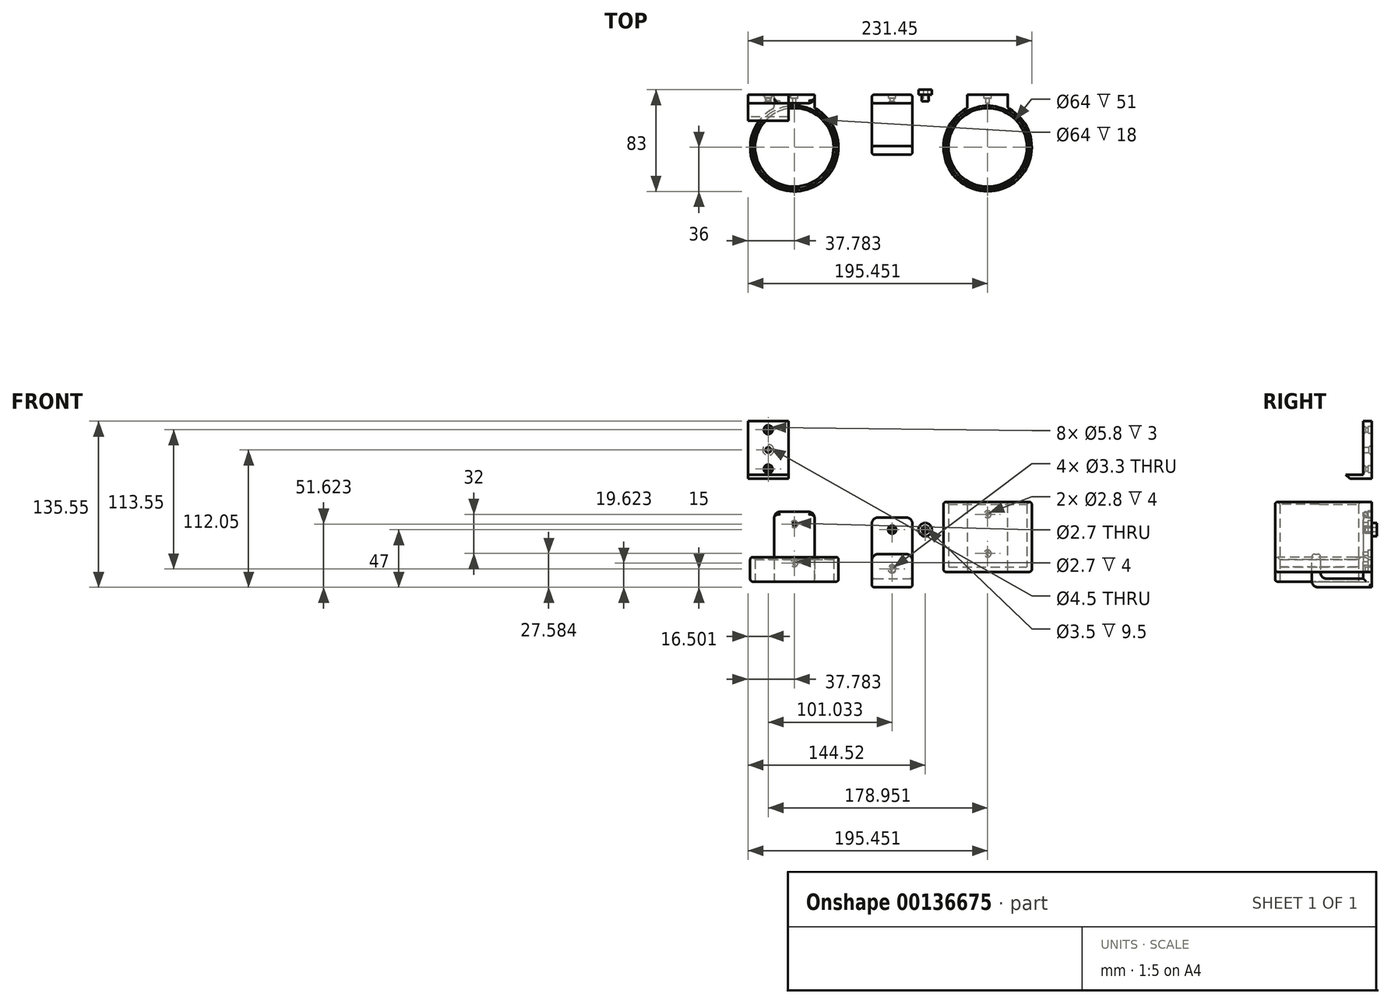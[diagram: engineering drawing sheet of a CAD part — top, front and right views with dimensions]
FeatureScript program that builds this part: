
annotation { "Feature Type Name" : "Feature", "Feature Type Description" : "" }
export const myFeature = defineFeature(function(context is Context, id is Id, definition is map)
    precondition{}
    {
        {
            var Q0;
            Q0=qCreatedBy(makeId("Front.planeOp"),FACE);
            var sketch = newSketch(context, id + "F0", { "sketchPlane" : qUnion([Q0])});
            skCircle(sketch, "E0", {"center": v(0, 0) * mm, "radius": 5.5 * mm});
            skCircle(sketch, "E1", {"center": v(0, 0) * mm, "radius": 2.75 * mm});
            skSolve(sketch);
        }
        {
            var Q0;
            Q0=makeQuery(id+"F0.imprint","IMPRINT",FACE,{"disambiguationData":[TD([[makeQuery(id+"F0.imprint","IMPRINT",EDGE,{"derivedFrom":sQuery(id+"F0.wireOp",EDGE,"E0")}),1.0]])]});
            var Q1;
            Q1=makeQuery(id+"F0.imprint","IMPRINT",FACE,{"disambiguationData":[TD([[makeQuery(id+"F0.imprint","IMPRINT",EDGE,{"derivedFrom":sQuery(id+"F0.wireOp",EDGE,"E1")}),1.0]])]});
            extrude(context, id + "F1", {"entities" : qUnion([Q0, Q1]), "oppositeDirection" : true, "depth" : 4 * mm});
        }
        {
            var Q0;
            Q0=makeQuery(id+"F0.imprint","IMPRINT",FACE,{"disambiguationData":[TD([[makeQuery(id+"F0.imprint","IMPRINT",EDGE,{"derivedFrom":sQuery(id+"F0.wireOp",EDGE,"E1")}),1.0]])]});
            extrude(context, id + "F2", {"entities" : qUnion([Q0]), "operationType" : NewBodyOperationType.ADD, "depth" : 5.5 * mm});
        }
        {
            var Q0;
            Q0=makeQuery(id+"F2.opExtrude","CAP_FACE",FACE,{"disambiguationData":[OSD([sQuery(id+"F0.wireOp",EDGE,"E1")])],"isStart":false});
            var sketch = newSketch(context, id + "F3", { "sketchPlane" : qUnion([Q0])});
            skPoint(sketch, "E2", {"position": v(0, 0) * mm});
            skSolve(sketch);
        }
        {
            var Q0;
            Q0=sQuery(id+"F3.wireOp",VERTEX,"E2");
            var Q1;
            Q1=makeQuery(id+"F1.opExtrude","SWEPT_BODY",BODY,{"disambiguationData":[OSD([sQuery(id+"F0.wireOp",EDGE,"E0")])]});
            hole(context, id + "F4", {"style" : HoleStyle.SIMPLE, "endStyle" : HoleEndStyle.THROUGH, "holeDiameter" : 3.5 * mm, "locations" : qUnion([Q0]), "scope" : qUnion([Q1]), "isTappedThrough" : true});
        }
        {
            var Q0;
            Q0=qCreatedBy(makeId("Front.planeOp"),FACE);
            var sketch = newSketch(context, id + "F5", { "sketchPlane" : qUnion([Q0])});
            skPoint(sketch, "E3", {"position": v(-26.99, 0) * mm});
            skCircle(sketch, "E4", {"center": v(-26.99, 0) * mm, "radius": 2.9 * mm});
            skLineSegment(sketch, "E5.bottom", {"start": v(-43.49, 10) * mm, "end": v(-10.49, 10) * mm});
            skLineSegment(sketch, "E5.top", {"start": v(-43.49, -47) * mm, "end": v(-10.49, -47) * mm});
            skLineSegment(sketch, "E5.left", {"start": v(-43.49, 10) * mm, "end": v(-43.49, -47) * mm});
            skLineSegment(sketch, "E5.right", {"start": v(-10.49, 10) * mm, "end": v(-10.49, -47) * mm});
            skPoint(sketch, "E6", {"position": v(-26.99, 10) * mm});
            skCircle(sketch, "E7", {"center": v(-26.99, 0) * mm, "radius": 1.65 * mm});
            skPoint(sketch, "E8", {"position": v(-26.99, -32) * mm});
            skCircle(sketch, "E9", {"center": v(-26.99, -32) * mm, "radius": 1.65 * mm});
            skCircle(sketch, "E10", {"center": v(-26.99, -32) * mm, "radius": 2.9 * mm});
            skSolve(sketch);
        }
        {
            var Q0;
            Q0=makeQuery(id+"F5.imprint","IMPRINT",FACE,{"disambiguationData":[TD([[makeQuery(id+"F5.imprint","IMPRINT",EDGE,{"derivedFrom":sQuery(id+"F5.wireOp",EDGE,"E4")}),-1.0]])]});
            var Q1;
            Q1=makeQuery(id+"F5.imprint","IMPRINT",FACE,{"disambiguationData":[TD([[makeQuery(id+"F5.imprint","IMPRINT",EDGE,{"derivedFrom":sQuery(id+"F5.wireOp",EDGE,"E4")}),1.0]])]});
            var Q2;
            Q2=makeQuery(id+"F5.imprint","IMPRINT",FACE,{"disambiguationData":[TD([[makeQuery(id+"F5.imprint","IMPRINT",EDGE,{"derivedFrom":sQuery(id+"F5.wireOp",EDGE,"E9")}),-1.0]])]});
            extrude(context, id + "F6", {"entities" : qUnion([Q0, Q1, Q2]), "depth" : 7 * mm});
        }
        {
            var Q0;
            Q0=makeQuery(id+"F5.imprint","IMPRINT",FACE,{"disambiguationData":[TD([[makeQuery(id+"F5.imprint","IMPRINT",EDGE,{"derivedFrom":sQuery(id+"F5.wireOp",EDGE,"E4")}),1.0]])]});
            var Q1;
            Q1=makeQuery(id+"F5.imprint","IMPRINT",FACE,{"disambiguationData":[TD([[makeQuery(id+"F5.imprint","IMPRINT",EDGE,{"derivedFrom":sQuery(id+"F5.wireOp",EDGE,"E9")}),-1.0]])]});
            extrude(context, id + "F7", {"entities" : qUnion([Q0, Q1]), "operationType" : NewBodyOperationType.REMOVE, "depth" : 3 * mm});
        }
        {
            var Q0;
            Q0=makeQuery(id+"F6.opExtrude","SWEPT_FACE",FACE,{"disambiguationData":[OSD([sQuery(id+"F5.wireOp",EDGE,"E5.right")])]});
            var sketch = newSketch(context, id + "F8", { "sketchPlane" : qUnion([Q0])});
            skLineSegment(sketch, "E11", {"start": v(-7, -47) * mm, "end": v(-49, -47) * mm});
            skLineSegment(sketch, "E12", {"start": v(-49, -47) * mm, "end": v(-49, -20) * mm});
            skLineSegment(sketch, "E13", {"start": v(-49, -20) * mm, "end": v(-42, -20) * mm});
            skLineSegment(sketch, "E14", {"start": v(-42, -20) * mm, "end": v(-42, -40) * mm});
            skLineSegment(sketch, "E15", {"start": v(-42, -40) * mm, "end": v(-7, -40) * mm});
            skSolve(sketch);
        }
        {
            var Q0;
            {var subQ0=sQuery(id+"F8.wireOp",EDGE,"E11");Q0=makeQuery(id+"F8.imprint","IMPRINT",FACE,{"disambiguationData":[TD([[makeQuery(id+"F8.imprint","IMPRINT",EDGE,{"derivedFrom":subQ0}),-1.0]])]});}
            var Q1;
            Q1=makeQuery(id+"F6.opExtrude","SWEPT_FACE",FACE,{"disambiguationData":[OSD([sQuery(id+"F5.wireOp",EDGE,"E5.left")])]});
            extrude(context, id + "F9", {"entities" : qUnion([Q0]), "operationType" : NewBodyOperationType.ADD, "endBound" : BoundingType.UP_TO_SURFACE, "oppositeDirection" : true, "endBoundEntityFace" : qUnion([Q1]), "depth" : 25 * mm});
        }
        {
            var Q0;
            Q0=makeQuery(id+"F6.opExtrude","SWEPT_EDGE",EDGE,{"disambiguationData":[OSD([sQuery(id+"F5.wireOp",EDGE,"E5.bottom"),sQuery(id+"F5.wireOp",EDGE,"E5.left")])]});
            var Q1;
            Q1=makeQuery(id+"F6.opExtrude","SWEPT_EDGE",EDGE,{"disambiguationData":[OSD([sQuery(id+"F5.wireOp",EDGE,"E5.bottom"),sQuery(id+"F5.wireOp",EDGE,"E5.right")])]});
            var Q2;
            Q2=makeQuery(id+"F9.opExtrude","CAP_EDGE",EDGE,{"disambiguationData":[OSD([sQuery(id+"F8.wireOp",EDGE,"E13")])],"isStart":true});
            var Q3;
            Q3=makeQuery(id+"F9.opExtrude","CAP_EDGE",EDGE,{"disambiguationData":[OSD([sQuery(id+"F8.wireOp",EDGE,"E13")])],"isStart":false});
            var Q4;
            Q4=makeQuery(id+"F9.opExtrude","SWEPT_EDGE",EDGE,{"disambiguationData":[OSD([sQuery(id+"F8.wireOp",EDGE,"E11"),sQuery(id+"F8.wireOp",EDGE,"E12")])]});
            var Q5;
            Q5=makeQuery(id+"F9.opExtrude","SWEPT_EDGE",EDGE,{"disambiguationData":[OSD([sQuery(id+"F8.wireOp",EDGE,"E14"),sQuery(id+"F8.wireOp",EDGE,"E15")])]});
            var Q6;
            Q6=makeQuery(id+"F9.opExtrude","SWEPT_EDGE",EDGE,{"disambiguationData":[OSD([sQuery(id+"F5.wireOp",EDGE,"E5.right"),sQuery(id+"F8.wireOp",EDGE,"E15")])]});
            fillet(context, id + "F10", {"entities" : qUnion([Q0, Q1, Q2, Q3, Q4, Q5, Q6]), "radius" : 5 * mm, "tangentPropagation" : true, "allowEdgeOverflow" : false});
        }
        {
            var Q0;
            Q0=makeQuery(id+"F9.boolean.opBoolean","MERGE",FACE,{"derivedFrom":[makeQuery(id+"F6.opExtrude","SWEPT_FACE",FACE,{"disambiguationData":[OSD([sQuery(id+"F5.wireOp",EDGE,"E5.left")])]}),makeQuery(id+"F9.opExtrude","CAP_FACE",FACE,{"disambiguationData":[OSD([sQuery(id+"F5.wireOp",EDGE,"E5.right"),sQuery(id+"F8.wireOp",EDGE,"E11"),sQuery(id+"F8.wireOp",EDGE,"E12"),sQuery(id+"F8.wireOp",EDGE,"E13"),sQuery(id+"F8.wireOp",EDGE,"E14"),sQuery(id+"F8.wireOp",EDGE,"E15")])],"isStart":false})]});
            fillet(context, id + "F11", {"entities" : qUnion([Q0]), "radius" : 2 * mm, "tangentPropagation" : true, "allowEdgeOverflow" : false});
        }
        {
            var Q0;
            Q0=makeQuery(id+"F6.opExtrude","CAP_EDGE",EDGE,{"disambiguationData":[OSD([sQuery(id+"F5.wireOp",EDGE,"E7")])],"isStart":false});
            var Q1;
            Q1=makeQuery(id+"F6.opExtrude","CAP_EDGE",EDGE,{"disambiguationData":[OSD([sQuery(id+"F5.wireOp",EDGE,"E9")])],"isStart":false});
            chamfer(context, id + "F12", {"entities" : qUnion([Q0, Q1]), "width" : 1.7 * mm, "tangentPropagation" : true});
        }
        {
            var Q0;
            Q0=qCreatedBy(makeId("Front.planeOp"),FACE);
            var sketch = newSketch(context, id + "F13", { "sketchPlane" : qUnion([Q0])});
            skPoint(sketch, "E16", {"position": v(50.93, 12.58) * mm});
            skCircle(sketch, "E17", {"center": v(50.93, 12.58) * mm, "radius": 2.9 * mm});
            skLineSegment(sketch, "E18.bottom", {"start": v(34.43, 22.58) * mm, "end": v(67.43, 22.58) * mm});
            skLineSegment(sketch, "E18.top", {"start": v(34.43, -34.42) * mm, "end": v(67.43, -34.42) * mm});
            skLineSegment(sketch, "E18.left", {"start": v(34.43, 22.58) * mm, "end": v(34.43, -34.42) * mm});
            skLineSegment(sketch, "E18.right", {"start": v(67.43, 22.58) * mm, "end": v(67.43, -34.42) * mm});
            skPoint(sketch, "E19", {"position": v(50.93, 22.58) * mm});
            skCircle(sketch, "E20", {"center": v(50.93, 12.58) * mm, "radius": 1.4 * mm});
            skPoint(sketch, "E21", {"position": v(50.93, -19.42) * mm});
            skCircle(sketch, "E22", {"center": v(50.93, -19.42) * mm, "radius": 1.4 * mm});
            skCircle(sketch, "E23", {"center": v(50.93, -19.42) * mm, "radius": 2.9 * mm});
            skSolve(sketch);
        }
        {
            var Q0;
            Q0=makeQuery(id+"F13.imprint","IMPRINT",FACE,{"disambiguationData":[TD([[makeQuery(id+"F13.imprint","IMPRINT",EDGE,{"derivedFrom":sQuery(id+"F13.wireOp",EDGE,"E17")}),1.0]])]});
            var Q1;
            Q1=makeQuery(id+"F13.imprint","IMPRINT",FACE,{"disambiguationData":[TD([[makeQuery(id+"F13.imprint","IMPRINT",EDGE,{"derivedFrom":sQuery(id+"F13.wireOp",EDGE,"E17")}),-1.0]])]});
            var Q2;
            Q2=makeQuery(id+"F13.imprint","IMPRINT",FACE,{"disambiguationData":[TD([[makeQuery(id+"F13.imprint","IMPRINT",EDGE,{"derivedFrom":sQuery(id+"F13.wireOp",EDGE,"E22")}),-1.0]])]});
            extrude(context, id + "F14", {"entities" : qUnion([Q0, Q1, Q2]), "depth" : 7 * mm});
        }
        {
            var Q0;
            Q0=makeQuery(id+"F13.imprint","IMPRINT",FACE,{"disambiguationData":[TD([[makeQuery(id+"F13.imprint","IMPRINT",EDGE,{"derivedFrom":sQuery(id+"F13.wireOp",EDGE,"E17")}),1.0]])]});
            var Q1;
            Q1=makeQuery(id+"F13.imprint","IMPRINT",FACE,{"disambiguationData":[TD([[makeQuery(id+"F13.imprint","IMPRINT",EDGE,{"derivedFrom":sQuery(id+"F13.wireOp",EDGE,"E22")}),-1.0]])]});
            extrude(context, id + "F15", {"entities" : qUnion([Q0, Q1]), "operationType" : NewBodyOperationType.REMOVE, "depth" : 3 * mm});
        }
        {
            var Q0;
            Q0=makeQuery(id+"F14.opExtrude","SWEPT_FACE",FACE,{"disambiguationData":[OSD([sQuery(id+"F13.wireOp",EDGE,"E18.top")])]});
            var sketch = newSketch(context, id + "F16", { "sketchPlane" : qUnion([Q0])});
            skPoint(sketch, "E24", {"position": v(50.93, 7) * mm});
            skCircle(sketch, "E25", {"center": v(50.93, 43) * mm, "radius": 36 * mm});
            skCircle(sketch, "E26", {"center": v(50.93, 43) * mm, "radius": 32 * mm});
            skLineSegment(sketch, "E27", {"start": v(50.93, 7) * mm, "end": v(34.43, 7) * mm});
            skLineSegment(sketch, "E28", {"start": v(34.43, 7) * mm, "end": v(34.43, 11) * mm});
            skLineSegment(sketch, "E29", {"start": v(67.43, 7) * mm, "end": v(67.43, 11) * mm});
            skLineSegment(sketch, "E30", {"start": v(50.93, 7) * mm, "end": v(67.43, 7) * mm});
            skSolve(sketch);
        }
        {
            var Q0;
            {var subQ2=sQuery(id+"F16.wireOp",EDGE,"E29");Q0=makeQuery(id+"F16.imprint","IMPRINT",FACE,{"disambiguationData":[TD([[makeQuery(id+"F16.imprint","IMPRINT",EDGE,{"derivedFrom":subQ2}),1.0]])]});}
            var Q1;
            Q1=makeQuery(id+"F16.imprint","IMPRINT",FACE,{"disambiguationData":[TD([[makeQuery(id+"F16.imprint","IMPRINT",EDGE,{"derivedFrom":sQuery(id+"F16.wireOp",EDGE,"E26")}),-1.0]])]});
            var Q2;
            {var subQ0=sQuery(id+"F16.wireOp",EDGE,"E27");Q2=makeQuery(id+"F16.imprint","IMPRINT",FACE,{"disambiguationData":[TD([[makeQuery(id+"F16.imprint","IMPRINT",EDGE,{"derivedFrom":subQ0}),1.0]])]});}
            var Q3;
            Q3=makeQuery(id+"F14.opExtrude","SWEPT_FACE",FACE,{"disambiguationData":[OSD([sQuery(id+"F13.wireOp",EDGE,"E18.bottom")])]});
            extrude(context, id + "F17", {"entities" : qUnion([Q0, Q1, Q2]), "operationType" : NewBodyOperationType.ADD, "endBound" : BoundingType.UP_TO_SURFACE, "oppositeDirection" : true, "endBoundEntityFace" : qUnion([Q3]), "depth" : 25 * mm});
        }
        {
            var Q0;
            Q0=makeQuery(id+"F16.imprint","IMPRINT",FACE,{"disambiguationData":[TD([[makeQuery(id+"F16.imprint","IMPRINT",EDGE,{"derivedFrom":sQuery(id+"F16.wireOp",EDGE,"E26")}),1.0]])]});
            extrude(context, id + "F18", {"entities" : qUnion([Q0]), "operationType" : NewBodyOperationType.ADD, "oppositeDirection" : true, "depth" : 4 * mm});
        }
        {
            var Q0;
            Q0=makeQuery(id+"F17.opExtrude","CAP_EDGE",EDGE,{"disambiguationData":[OSD([sQuery(id+"F16.wireOp",EDGE,"E26")])],"isStart":false});
            chamfer(context, id + "F19", {"entities" : qUnion([Q0]), "width" : 2 * mm, "tangentPropagation" : true});
        }
        {
            var Q0;
            Q0=makeQuery(id+"F17.opExtrude","CAP_EDGE",EDGE,{"disambiguationData":[OSD([sQuery(id+"F16.wireOp",EDGE,"E25")])],"isStart":false});
            var Q1;
            Q1=makeQuery(id+"F17.boolean.opBoolean","MERGE",EDGE,{"derivedFrom":[makeQuery(id+"F14.opExtrude","SWEPT_EDGE",EDGE,{"disambiguationData":[OSD([sQuery(id+"F13.wireOp",EDGE,"E18.bottom"),sQuery(id+"F13.wireOp",EDGE,"E18.right")])]}),makeQuery(id+"F17.opExtrude","CAP_EDGE",EDGE,{"disambiguationData":[OSD([sQuery(id+"F16.wireOp",EDGE,"E29")])],"isStart":false})]});
            var Q2;
            Q2=makeQuery(id+"F17.boolean.opBoolean","MERGE",EDGE,{"derivedFrom":[makeQuery(id+"F14.opExtrude","SWEPT_EDGE",EDGE,{"disambiguationData":[OSD([sQuery(id+"F13.wireOp",EDGE,"E18.bottom"),sQuery(id+"F13.wireOp",EDGE,"E18.left")])]}),makeQuery(id+"F17.opExtrude","CAP_EDGE",EDGE,{"disambiguationData":[OSD([sQuery(id+"F16.wireOp",EDGE,"E28")])],"isStart":false})]});
            var Q3;
            Q3=makeQuery(id+"F17.opExtrude","SWEPT_EDGE",EDGE,{"disambiguationData":[OSD([sQuery(id+"F16.wireOp",EDGE,"E25"),sQuery(id+"F16.wireOp",EDGE,"E29")])]});
            var Q4;
            Q4=makeQuery(id+"F17.opExtrude","SWEPT_EDGE",EDGE,{"disambiguationData":[OSD([sQuery(id+"F16.wireOp",EDGE,"E25"),sQuery(id+"F16.wireOp",EDGE,"E28")])]});
            var Q5;
            Q5=makeQuery(id+"F17.opExtrude","CAP_EDGE",EDGE,{"disambiguationData":[OSD([sQuery(id+"F16.wireOp",EDGE,"E25")])],"isStart":true});
            var Q6;
            Q6=makeQuery(id+"F17.boolean.opBoolean","MERGE",EDGE,{"derivedFrom":[makeQuery(id+"F14.opExtrude","SWEPT_EDGE",EDGE,{"disambiguationData":[OSD([sQuery(id+"F13.wireOp",EDGE,"E18.top"),sQuery(id+"F13.wireOp",EDGE,"E18.left")])]}),makeQuery(id+"F17.opExtrude","CAP_EDGE",EDGE,{"disambiguationData":[OSD([sQuery(id+"F16.wireOp",EDGE,"E28")])],"isStart":true})]});
            var Q7;
            Q7=makeQuery(id+"F17.boolean.opBoolean","MERGE",EDGE,{"derivedFrom":[makeQuery(id+"F14.opExtrude","SWEPT_EDGE",EDGE,{"disambiguationData":[OSD([sQuery(id+"F13.wireOp",EDGE,"E18.top"),sQuery(id+"F13.wireOp",EDGE,"E18.right")])]}),makeQuery(id+"F17.opExtrude","CAP_EDGE",EDGE,{"disambiguationData":[OSD([sQuery(id+"F16.wireOp",EDGE,"E29")])],"isStart":true})]});
            fillet(context, id + "F20", {"entities" : qUnion([Q0, Q1, Q2, Q3, Q4, Q5, Q6, Q7]), "radius" : 2 * mm, "tangentPropagation" : true, "allowEdgeOverflow" : false});
        }
        {
            var Q0;
            Q0=qCreatedBy(makeId("Front.planeOp"),FACE);
            var sketch = newSketch(context, id + "F21", { "sketchPlane" : qUnion([Q0])});
            skPoint(sketch, "E31", {"position": v(-106.74, 4.62) * mm});
            skCircle(sketch, "E32", {"center": v(-106.74, 4.62) * mm, "radius": 2.9 * mm});
            skLineSegment(sketch, "E33.bottom", {"start": v(-123.24, 14.62) * mm, "end": v(-90.24, 14.62) * mm});
            skLineSegment(sketch, "E33.top", {"start": v(-123.24, -42.38) * mm, "end": v(-90.24, -42.38) * mm});
            skLineSegment(sketch, "E33.left", {"start": v(-123.24, 14.62) * mm, "end": v(-123.24, -42.38) * mm});
            skLineSegment(sketch, "E33.right", {"start": v(-90.24, 14.62) * mm, "end": v(-90.24, -42.38) * mm});
            skPoint(sketch, "E34", {"position": v(-106.74, 14.62) * mm});
            skCircle(sketch, "E35", {"center": v(-106.74, 4.62) * mm, "radius": 1.35 * mm});
            skPoint(sketch, "E36", {"position": v(-106.74, -27.38) * mm});
            skCircle(sketch, "E37", {"center": v(-106.74, -27.38) * mm, "radius": 1.35 * mm});
            skCircle(sketch, "E38", {"center": v(-106.74, -27.38) * mm, "radius": 2.9 * mm});
            skSolve(sketch);
        }
        {
            var Q0;
            Q0 = qSketchRegion(id + "F21", true);
            var Q1;
            Q1=makeQuery(id+"F21.imprint","IMPRINT",FACE,{"disambiguationData":[TD([[makeQuery(id+"F21.imprint","IMPRINT",EDGE,{"derivedFrom":sQuery(id+"F21.wireOp",EDGE,"E32")}),-1.0]])]});
            var Q2;
            Q2=makeQuery(id+"F21.imprint","IMPRINT",FACE,{"disambiguationData":[TD([[makeQuery(id+"F21.imprint","IMPRINT",EDGE,{"derivedFrom":sQuery(id+"F21.wireOp",EDGE,"E37")}),-1.0]])]});
            var Q3;
            Q3=makeQuery(id+"F21.imprint","IMPRINT",FACE,{"disambiguationData":[TD([[makeQuery(id+"F21.imprint","IMPRINT",EDGE,{"derivedFrom":sQuery(id+"F21.wireOp",EDGE,"E32")}),1.0]])]});
            extrude(context, id + "F22", {"entities" : qUnion([Q0, Q1, Q2, Q3]), "depth" : 7 * mm});
        }
        {
            var Q0;
            Q0=makeQuery(id+"F21.imprint","IMPRINT",FACE,{"disambiguationData":[TD([[makeQuery(id+"F21.imprint","IMPRINT",EDGE,{"derivedFrom":sQuery(id+"F21.wireOp",EDGE,"E32")}),1.0]])]});
            var Q1;
            Q1=makeQuery(id+"F21.imprint","IMPRINT",FACE,{"disambiguationData":[TD([[makeQuery(id+"F21.imprint","IMPRINT",EDGE,{"derivedFrom":sQuery(id+"F21.wireOp",EDGE,"E37")}),-1.0]])]});
            extrude(context, id + "F23", {"entities" : qUnion([Q0, Q1]), "operationType" : NewBodyOperationType.REMOVE, "depth" : 3 * mm});
        }
        {
            var Q0;
            Q0=makeQuery(id+"F22.opExtrude","SWEPT_FACE",FACE,{"disambiguationData":[OSD([sQuery(id+"F21.wireOp",EDGE,"E33.top")])]});
            var sketch = newSketch(context, id + "F24", { "sketchPlane" : qUnion([Q0])});
            skCircle(sketch, "E39", {"center": v(-106.74, 43) * mm, "radius": 36 * mm});
            skPoint(sketch, "E39.centerSnap0", {"position": v(-106.74, 7) * mm});
            skCircle(sketch, "E40", {"center": v(-106.74, 43) * mm, "radius": 32 * mm});
            skLineSegment(sketch, "E41", {"start": v(-90.24, 7) * mm, "end": v(-123.24, 7) * mm});
            skLineSegment(sketch, "E42", {"start": v(-123.24, 7) * mm, "end": v(-123.24, 11) * mm});
            skLineSegment(sketch, "E43", {"start": v(-90.24, 7) * mm, "end": v(-90.24, 11) * mm});
            skSolve(sketch);
        }
        {
            var Q0;
            Q0=makeQuery(id+"F24.imprint","IMPRINT",FACE,{"disambiguationData":[TD([[makeQuery(id+"F24.imprint","IMPRINT",EDGE,{"derivedFrom":sQuery(id+"F24.wireOp",EDGE,"E40")}),-1.0]])]});
            var Q1;
            {var subQ0=sQuery(id+"F24.wireOp",EDGE,"E42");Q1=makeQuery(id+"F24.imprint","IMPRINT",FACE,{"disambiguationData":[TD([[makeQuery(id+"F24.imprint","IMPRINT",EDGE,{"derivedFrom":subQ0}),-1.0]])]});}
            var Q2;
            {var subQ0=sQuery(id+"F24.wireOp",EDGE,"E43");Q2=makeQuery(id+"F24.imprint","IMPRINT",FACE,{"disambiguationData":[TD([[makeQuery(id+"F24.imprint","IMPRINT",EDGE,{"derivedFrom":subQ0}),1.0]])]});}
            extrude(context, id + "F25", {"entities" : qUnion([Q0, Q1, Q2]), "operationType" : NewBodyOperationType.ADD, "oppositeDirection" : true, "depth" : 20 * mm});
        }
        {
            var Q0;
            Q0=makeQuery(id+"F25.opExtrude","CAP_EDGE",EDGE,{"disambiguationData":[OSD([sQuery(id+"F24.wireOp",EDGE,"E40")])],"isStart":false});
            chamfer(context, id + "F26", {"entities" : qUnion([Q0]), "width" : 2 * mm, "tangentPropagation" : true});
        }
        {
            var Q0;
            Q0=makeQuery(id+"F25.opExtrude","CAP_EDGE",EDGE,{"disambiguationData":[OSD([sQuery(id+"F24.wireOp",EDGE,"E39")])],"isStart":false});
            var Q1;
            Q1=makeQuery(id+"F25.opExtrude","CAP_EDGE",EDGE,{"disambiguationData":[OSD([sQuery(id+"F24.wireOp",EDGE,"E43")])],"isStart":false});
            var Q2;
            Q2=makeQuery(id+"F25.opExtrude","CAP_EDGE",EDGE,{"disambiguationData":[OSD([sQuery(id+"F24.wireOp",EDGE,"E42")])],"isStart":false});
            var Q3;
            Q3=makeQuery(id+"F25.opExtrude","CAP_EDGE",EDGE,{"disambiguationData":[OSD([sQuery(id+"F24.wireOp",EDGE,"E41")])],"isStart":false});
            var Q4;
            Q4=makeQuery(id+"F22.opExtrude","CAP_EDGE",EDGE,{"disambiguationData":[OSD([sQuery(id+"F21.wireOp",EDGE,"E33.bottom")])],"isStart":false});
            var Q5;
            Q5=makeQuery(id+"F25.opExtrude","CAP_EDGE",EDGE,{"disambiguationData":[OSD([sQuery(id+"F24.wireOp",EDGE,"E39")])],"isStart":true});
            var Q6;
            Q6=makeQuery(id+"F25.boolean.opBoolean","MERGE",EDGE,{"derivedFrom":[makeQuery(id+"F22.opExtrude","SWEPT_EDGE",EDGE,{"disambiguationData":[OSD([sQuery(id+"F21.wireOp",EDGE,"E33.top"),sQuery(id+"F21.wireOp",EDGE,"E33.right")])]}),makeQuery(id+"F25.opExtrude","CAP_EDGE",EDGE,{"disambiguationData":[OSD([sQuery(id+"F24.wireOp",EDGE,"E43")])],"isStart":true})]});
            var Q7;
            Q7=makeQuery(id+"F25.boolean.opBoolean","MERGE",EDGE,{"derivedFrom":[makeQuery(id+"F22.opExtrude","SWEPT_EDGE",EDGE,{"disambiguationData":[OSD([sQuery(id+"F21.wireOp",EDGE,"E33.top"),sQuery(id+"F21.wireOp",EDGE,"E33.left")])]}),makeQuery(id+"F25.opExtrude","CAP_EDGE",EDGE,{"disambiguationData":[OSD([sQuery(id+"F24.wireOp",EDGE,"E42")])],"isStart":true})]});
            var Q8;
            Q8=makeQuery(id+"F25.opExtrude","SWEPT_EDGE",EDGE,{"disambiguationData":[OSD([sQuery(id+"F24.wireOp",EDGE,"E39"),sQuery(id+"F24.wireOp",EDGE,"E42")])]});
            var Q9;
            Q9=makeQuery(id+"F25.opExtrude","SWEPT_EDGE",EDGE,{"disambiguationData":[OSD([sQuery(id+"F24.wireOp",EDGE,"E39"),sQuery(id+"F24.wireOp",EDGE,"E43")])]});
            fillet(context, id + "F27", {"entities" : qUnion([Q0, Q1, Q2, Q3, Q4, Q5, Q6, Q7, Q8, Q9]), "radius" : 2 * mm, "tangentPropagation" : true, "allowEdgeOverflow" : false});
        }
        {
            var Q0;
            Q0=makeQuery(id+"F22.opExtrude","SWEPT_EDGE",EDGE,{"disambiguationData":[OSD([sQuery(id+"F21.wireOp",EDGE,"E33.bottom"),sQuery(id+"F21.wireOp",EDGE,"E33.right")])]});
            var Q1;
            Q1=makeQuery(id+"F22.opExtrude","SWEPT_EDGE",EDGE,{"disambiguationData":[OSD([sQuery(id+"F21.wireOp",EDGE,"E33.bottom"),sQuery(id+"F21.wireOp",EDGE,"E33.left")])]});
            fillet(context, id + "F28", {"entities" : qUnion([Q0, Q1]), "radius" : 5 * mm, "tangentPropagation" : true, "allowEdgeOverflow" : false});
        }
        {
            var Q0;
            Q0=qCreatedBy(makeId("Front.planeOp"),FACE);
            var sketch = newSketch(context, id + "F29", { "sketchPlane" : qUnion([Q0])});
            skPoint(sketch, "E44", {"position": v(-128.02, 81.55) * mm});
            skCircle(sketch, "E45", {"center": v(-128.02, 81.55) * mm, "radius": 2.9 * mm});
            skLineSegment(sketch, "E46.bottom", {"start": v(-144.52, 88.55) * mm, "end": v(-111.52, 88.55) * mm});
            skLineSegment(sketch, "E46.top", {"start": v(-144.52, 41.55) * mm, "end": v(-111.52, 41.55) * mm});
            skLineSegment(sketch, "E46.left", {"start": v(-144.52, 88.55) * mm, "end": v(-144.52, 41.55) * mm});
            skLineSegment(sketch, "E46.right", {"start": v(-111.52, 88.55) * mm, "end": v(-111.52, 41.55) * mm});
            skPoint(sketch, "E47", {"position": v(-128.02, 88.55) * mm});
            skCircle(sketch, "E48", {"center": v(-128.02, 81.55) * mm, "radius": 1.65 * mm});
            skPoint(sketch, "E49", {"position": v(-128.02, 49.55) * mm});
            skCircle(sketch, "E50", {"center": v(-128.02, 49.55) * mm, "radius": 1.65 * mm});
            skCircle(sketch, "E51", {"center": v(-128.02, 49.55) * mm, "radius": 2.9 * mm});
            skLineSegment(sketch, "E52", {"start": v(-144.52, 44.9) * mm, "end": v(-111.52, 44.9) * mm});
            skPoint(sketch, "E53", {"position": v(-128.02, 65.05) * mm});
            skPoint(sketch, "E53.positionSnap0", {"position": v(-111.52, 65.05) * mm});
            skSolve(sketch);
        }
        {
            var Q0;
            Q0=makeQuery(id+"F29.imprint","IMPRINT",FACE,{"disambiguationData":[TD([[makeQuery(id+"F29.imprint","IMPRINT",EDGE,{"derivedFrom":sQuery(id+"F29.wireOp",EDGE,"E45")}),-1.0]])]});
            var Q1;
            Q1=makeQuery(id+"F29.imprint","IMPRINT",FACE,{"disambiguationData":[TD([[makeQuery(id+"F29.imprint","IMPRINT",EDGE,{"derivedFrom":sQuery(id+"F29.wireOp",EDGE,"E50")}),-1.0]])]});
            var Q2;
            Q2=makeQuery(id+"F29.imprint","IMPRINT",FACE,{"disambiguationData":[TD([[makeQuery(id+"F29.imprint","IMPRINT",EDGE,{"derivedFrom":sQuery(id+"F29.wireOp",EDGE,"E45")}),1.0]])]});
            var Q3;
            {var subQ4=sQuery(id+"F29.wireOp",EDGE,"E46.top");Q3=makeQuery(id+"F29.imprint","IMPRINT",FACE,{"disambiguationData":[TD([[makeQuery(id+"F29.imprint","IMPRINT",EDGE,{"derivedFrom":subQ4}),1.0]])]});}
            extrude(context, id + "F30", {"entities" : qUnion([Q0, Q1, Q2, Q3]), "depth" : 7 * mm});
        }
        {
            var Q0;
            Q0=makeQuery(id+"F29.imprint","IMPRINT",FACE,{"disambiguationData":[TD([[makeQuery(id+"F29.imprint","IMPRINT",EDGE,{"derivedFrom":sQuery(id+"F29.wireOp",EDGE,"E45")}),1.0]])]});
            var Q1;
            Q1=makeQuery(id+"F29.imprint","IMPRINT",FACE,{"disambiguationData":[TD([[makeQuery(id+"F29.imprint","IMPRINT",EDGE,{"derivedFrom":sQuery(id+"F29.wireOp",EDGE,"E50")}),-1.0]])]});
            extrude(context, id + "F31", {"entities" : qUnion([Q0, Q1]), "operationType" : NewBodyOperationType.REMOVE, "depth" : 3 * mm});
        }
        {
            var Q0;
            {var subQ4=sQuery(id+"F29.wireOp",EDGE,"E46.top");Q0=makeQuery(id+"F29.imprint","IMPRINT",FACE,{"disambiguationData":[TD([[makeQuery(id+"F29.imprint","IMPRINT",EDGE,{"derivedFrom":subQ4}),1.0]])]});}
            extrude(context, id + "F32", {"entities" : qUnion([Q0]), "operationType" : NewBodyOperationType.ADD, "depth" : 26 * mm});
        }
        {
            var Q0;
            Q0=makeQuery(id+"F32.opExtrude","CAP_EDGE",EDGE,{"disambiguationData":[OSD([sQuery(id+"F29.wireOp",EDGE,"E46.top")])],"isStart":false});
            chamfer(context, id + "F33", {"entities" : qUnion([Q0]), "width" : 8 * mm, "tangentPropagation" : true});
        }
        {
            var Q0;
            Q0=makeQuery(id+"F30.opExtrude","CAP_EDGE",EDGE,{"disambiguationData":[OSD([sQuery(id+"F29.wireOp",EDGE,"E48")])],"isStart":false});
            var Q1;
            Q1=makeQuery(id+"F30.opExtrude","CAP_EDGE",EDGE,{"disambiguationData":[OSD([sQuery(id+"F29.wireOp",EDGE,"E50")])],"isStart":false});
            chamfer(context, id + "F34", {"entities" : qUnion([Q0, Q1]), "width" : 2 * mm, "tangentPropagation" : true});
        }
        {
            var Q0;
            Q0=sQuery(id+"F29.wireOp",VERTEX,"E53");
            var Q1;
            Q1=makeQuery(id+"F30.opExtrude","SWEPT_BODY",BODY,{"disambiguationData":[OSD([sQuery(id+"F29.wireOp",EDGE,"E46.bottom"),sQuery(id+"F29.wireOp",EDGE,"E46.top"),sQuery(id+"F29.wireOp",EDGE,"E46.left"),sQuery(id+"F29.wireOp",EDGE,"E46.right"),sQuery(id+"F29.wireOp",EDGE,"E48"),sQuery(id+"F29.wireOp",EDGE,"E50")])]});
            hole(context, id + "F35", {"style" : HoleStyle.C_SINK, "endStyle" : HoleEndStyle.THROUGH, "oppositeDirection" : true, "standardTappedOrClearance" : lookupTablePath({ "standard" : "ANSI", "fit" : "Normal (ASME)", "size" : "#8", "type" : "Clearance" }), "standardBlindInLast" : lookupTablePath({ "fit" : "Free", "standard" : "ANSI", "size" : "#8", "type" : "Clearance" }), "holeDiameter" : 4.5 * mm, "cSinkDiameter" : 9.12 * mm, "cSinkAngle" : 82 * degree, "locations" : qUnion([Q0]), "scope" : qUnion([Q1]), "isTappedThrough" : true});
        }
    });
